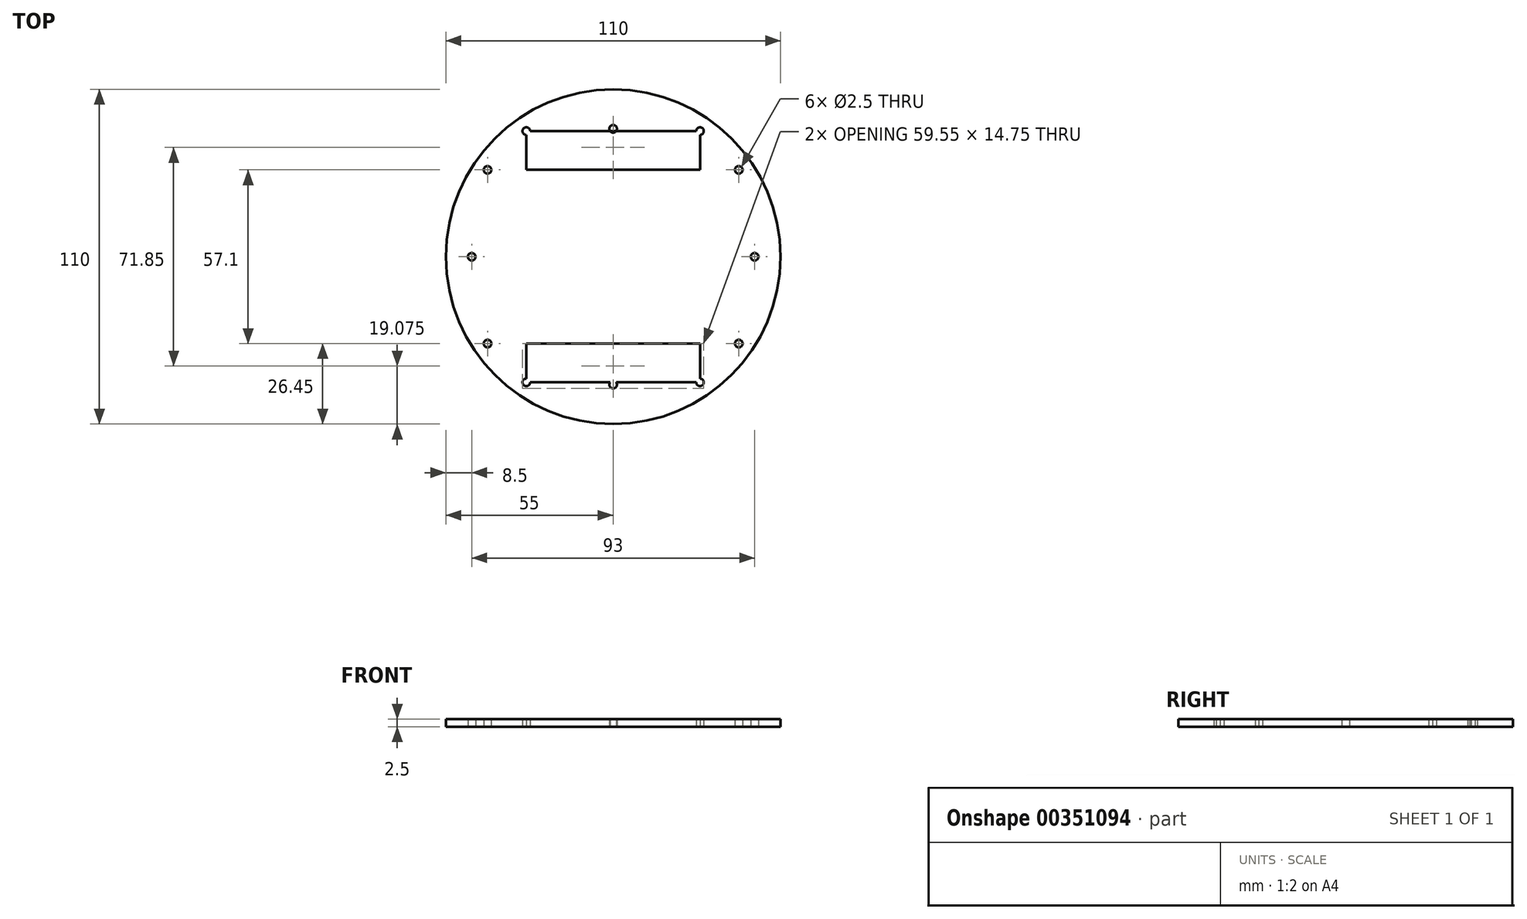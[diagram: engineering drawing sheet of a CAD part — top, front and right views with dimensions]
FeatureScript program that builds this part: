
annotation { "Feature Type Name" : "Feature", "Feature Type Description" : "" }
export const myFeature = defineFeature(function(context is Context, id is Id, definition is map)
    precondition{}
    {
        {
            var Q0;
            Q0=qCreatedBy(makeId("Top.planeOp"),FACE);
            var sketch = newSketch(context, id + "F0", { "sketchPlane" : qUnion([Q0])});
            skCircle(sketch, "E0", {"center": v(0, 0) * mm, "radius": 55 * mm});
            skCircle(sketch, "E1", {"center": v(46.5, 0) * mm, "radius": 1.25 * mm});
            skCircle(sketch, "E2", {"center": v(0, -42.05) * mm, "radius": 1.25 * mm});
            skCircle(sketch, "E3.MirrorC", {"center": v(-46.5, 0) * mm, "radius": 1.25 * mm});
            skCircle(sketch, "E4.MirrorC", {"center": v(0, 42.05) * mm, "radius": 1.25 * mm});
            skLineSegment(sketch, "E5.bottom", {"start": v(28.55, 41.3) * mm, "end": v(-28.55, 41.3) * mm});
            skLineSegment(sketch, "E5.top", {"start": v(28.55, -41.3) * mm, "end": v(-28.55, -41.3) * mm});
            skLineSegment(sketch, "E5.left", {"start": v(28.55, 41.3) * mm, "end": v(28.55, -41.3) * mm});
            skLineSegment(sketch, "E5.right", {"start": v(-28.55, 41.3) * mm, "end": v(-28.55, -41.3) * mm});
            skCircle(sketch, "E6", {"center": v(-28.55, 41.3) * mm, "radius": 1.25 * mm});
            skCircle(sketch, "E7.MirrorC", {"center": v(28.55, 41.3) * mm, "radius": 1.25 * mm});
            skCircle(sketch, "E8.MirrorC", {"center": v(-28.55, -41.3) * mm, "radius": 1.25 * mm});
            skCircle(sketch, "E9.MirrorC", {"center": v(28.55, -41.3) * mm, "radius": 1.25 * mm});
            skLineSegment(sketch, "E10.bottom", {"start": v(41.3, 28.55) * mm, "end": v(-41.3, 28.55) * mm});
            skLineSegment(sketch, "E10.top", {"start": v(41.3, -28.55) * mm, "end": v(-41.3, -28.55) * mm});
            skLineSegment(sketch, "E10.left", {"start": v(41.3, 28.55) * mm, "end": v(41.3, -28.55) * mm});
            skLineSegment(sketch, "E10.right", {"start": v(-41.3, 28.55) * mm, "end": v(-41.3, -28.55) * mm});
            skCircle(sketch, "E11", {"center": v(-41.3, 28.55) * mm, "radius": 1.25 * mm});
            skCircle(sketch, "E12.MirrorC", {"center": v(41.3, 28.55) * mm, "radius": 1.25 * mm});
            skCircle(sketch, "E13.MirrorC", {"center": v(-41.3, -28.55) * mm, "radius": 1.25 * mm});
            skCircle(sketch, "E14.MirrorC", {"center": v(41.3, -28.55) * mm, "radius": 1.25 * mm});
            skSolve(sketch);
        }
        {
            var Q0;
            Q0=makeQuery(id+"F0.imprint","IMPRINT",FACE,{"disambiguationData":[TD([[makeQuery(id+"F0.imprint","IMPRINT",EDGE,{"derivedFrom":sQuery(id+"F0.wireOp",EDGE,"E0")}),1.0]])]});
            var Q1;
            {var subQ5=sQuery(id+"F0.wireOp",EDGE,"E5.bottom");var subQ6=sQuery(id+"F0.wireOp",EDGE,"E4.MirrorC");var subQ7=makeQuery(id+"F0.imprint","INTERSECT",VERTEX,{"disambiguationData":[OD(0.0)],"derivedFrom":[subQ6,subQ5]});Q1=makeQuery(id+"F0.imprint","IMPRINT",FACE,{"disambiguationData":[TD([[makeQuery(id+"F0.imprint","IMPRINT",EDGE,{"disambiguationData":[TD([[subQ7,-1.0]])],"derivedFrom":subQ6}),1.0]])]});}
            var Q2;
            {var subQ0=sQuery(id+"F0.wireOp",EDGE,"E10.bottom");var subQ1=sQuery(id+"F0.wireOp",EDGE,"E5.left");var subQ2=makeQuery(id+"F0.imprint","INTERSECT",VERTEX,{"derivedFrom":[subQ1,subQ0]});Q2=makeQuery(id+"F0.imprint","IMPRINT",FACE,{"disambiguationData":[TD([[makeQuery(id+"F0.imprint","IMPRINT",EDGE,{"disambiguationData":[TD([[subQ2,-1.0]])],"derivedFrom":subQ1}),-1.0]])]});}
            var Q3;
            {var subQ1=sQuery(id+"F0.wireOp",EDGE,"E5.right");var subQ5=sQuery(id+"F0.wireOp",EDGE,"E10.bottom");var subQ6=makeQuery(id+"F0.imprint","INTERSECT",VERTEX,{"derivedFrom":[subQ1,subQ5]});Q3=makeQuery(id+"F0.imprint","IMPRINT",FACE,{"disambiguationData":[TD([[makeQuery(id+"F0.imprint","IMPRINT",EDGE,{"disambiguationData":[TD([[subQ6,-1.0]])],"derivedFrom":subQ1}),-1.0]])]});}
            var Q4;
            {var subQ7=sQuery(id+"F0.wireOp",EDGE,"E5.top");var subQ8=sQuery(id+"F0.wireOp",EDGE,"E2");var subQ12=makeQuery(id+"F0.imprint","INTERSECT",VERTEX,{"disambiguationData":[OD(0.0)],"derivedFrom":[subQ8,subQ7]});Q4=makeQuery(id+"F0.imprint","IMPRINT",FACE,{"disambiguationData":[TD([[makeQuery(id+"F0.imprint","IMPRINT",EDGE,{"disambiguationData":[TD([[subQ12,-1.0]])],"derivedFrom":subQ8}),-1.0]])]});}
            var Q5;
            {var subQ6=sQuery(id+"F0.wireOp",EDGE,"E5.left");var subQ9=sQuery(id+"F0.wireOp",EDGE,"E10.bottom");var subQ10=makeQuery(id+"F0.imprint","INTERSECT",VERTEX,{"derivedFrom":[subQ6,subQ9]});Q5=makeQuery(id+"F0.imprint","IMPRINT",FACE,{"disambiguationData":[TD([[makeQuery(id+"F0.imprint","IMPRINT",EDGE,{"disambiguationData":[TD([[subQ10,-1.0]])],"derivedFrom":subQ6}),1.0]])]});}
            extrude(context, id + "F1", {"entities" : qUnion([Q0, Q1, Q2, Q3, Q4, Q5]), "depth" : 2.5 * mm});
        }
    });
